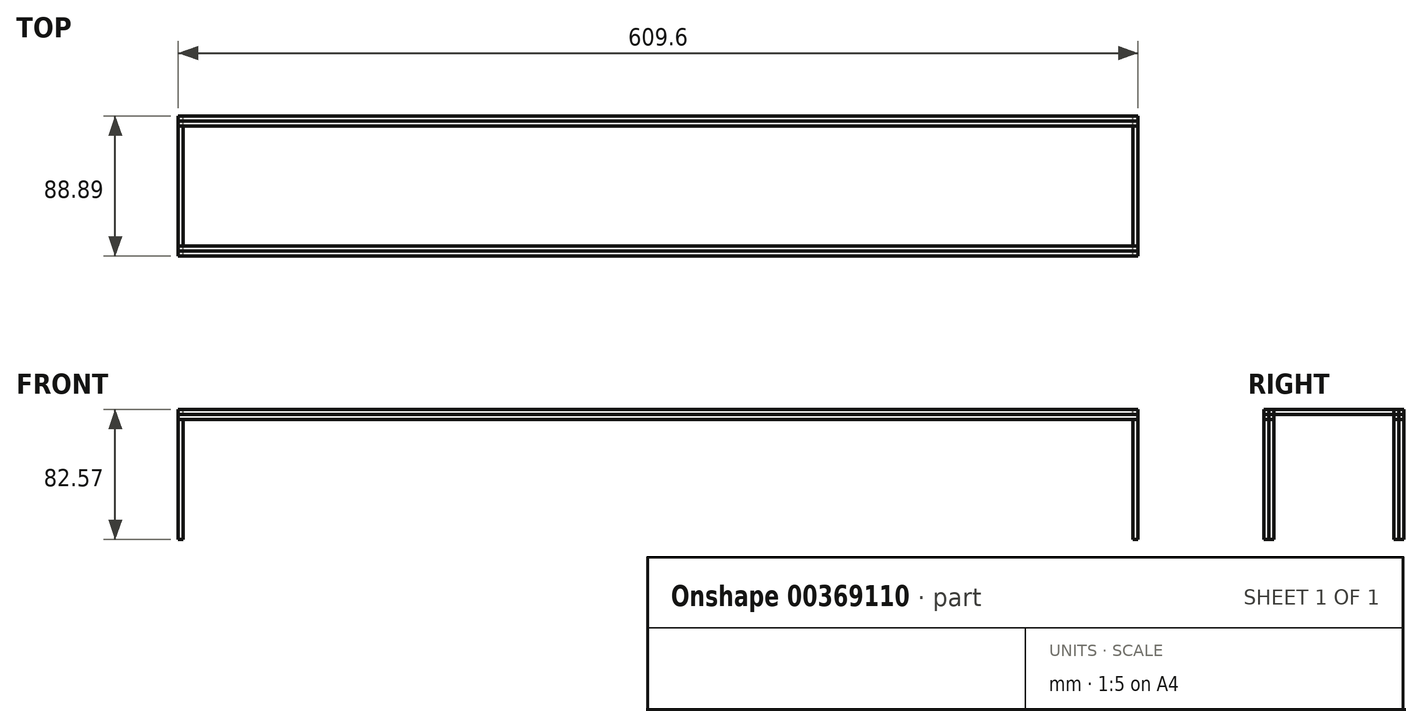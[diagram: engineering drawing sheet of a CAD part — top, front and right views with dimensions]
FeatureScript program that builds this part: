
annotation { "Feature Type Name" : "Feature", "Feature Type Description" : "" }
export const myFeature = defineFeature(function(context is Context, id is Id, definition is map)
    precondition{}
    {
        {
            var Q0;
            Q0=qCreatedBy(makeId("Front.planeOp"),FACE);
            var sketch = newSketch(context, id + "F0", { "sketchPlane" : qUnion([Q0])});
            skLineSegment(sketch, "E0.bottom", {"start": v(-296.3, -78.86) * mm, "end": v(313.3, -78.86) * mm});
            skLineSegment(sketch, "E0.top", {"start": v(-296.3, -75.69) * mm, "end": v(313.3, -75.69) * mm});
            skLineSegment(sketch, "E0.left", {"start": v(-296.3, -78.86) * mm, "end": v(-296.3, -75.69) * mm});
            skLineSegment(sketch, "E0.right", {"start": v(313.3, -78.86) * mm, "end": v(313.3, -75.69) * mm});
            skSolve(sketch);
        }
        {
            var Q0;
            Q0 = qSketchRegion(id + "F0", true);
            extrude(context, id + "F1", {"entities" : qUnion([Q0]), "depth" : 3.17 * mm});
        }
        {
            var Q0;
            Q0=makeQuery(id+"F1.opExtrude","SWEPT_BODY",BODY,{"disambiguationData":[OSD([sQuery(id+"F0.wireOp",EDGE,"E0.bottom"),sQuery(id+"F0.wireOp",EDGE,"E0.top"),sQuery(id+"F0.wireOp",EDGE,"E0.left"),sQuery(id+"F0.wireOp",EDGE,"E0.right")])]});
            transform(context, id + "F2", {"entities" : qUnion([Q0]), "transformType" : TransformType.TRANSLATION_3D, "dx" : 0 * mm, "dy" : 3.17 * mm, "dz" : 0 * mm, "makeCopy" : true});
        }
        {
            var Q0;
            Q0=makeQuery(id+"F1.opExtrude","SWEPT_BODY",BODY,{"disambiguationData":[OSD([sQuery(id+"F0.wireOp",EDGE,"E0.bottom"),sQuery(id+"F0.wireOp",EDGE,"E0.top"),sQuery(id+"F0.wireOp",EDGE,"E0.left"),sQuery(id+"F0.wireOp",EDGE,"E0.right")])]});
            transform(context, id + "F3", {"entities" : qUnion([Q0]), "transformType" : TransformType.TRANSLATION_3D, "dx" : 0 * mm, "dy" : 3.17 * mm, "dz" : 0 * mm, "makeCopy" : true});
        }
        {
            var Q0;
            Q0=makeQuery(id+"F1.opExtrude","SWEPT_BODY",BODY,{"disambiguationData":[OSD([sQuery(id+"F0.wireOp",EDGE,"E0.bottom"),sQuery(id+"F0.wireOp",EDGE,"E0.top"),sQuery(id+"F0.wireOp",EDGE,"E0.left"),sQuery(id+"F0.wireOp",EDGE,"E0.right")])]});
            transform(context, id + "F4", {"entities" : qUnion([Q0]), "transformType" : TransformType.TRANSLATION_3D, "dx" : 0 * mm, "dy" : 3.17 * mm, "dz" : 0 * mm, "makeCopy" : true});
        }
        {
            var Q0;
            Q0=makeQuery(id+"F1.opExtrude","SWEPT_BODY",BODY,{"disambiguationData":[OSD([sQuery(id+"F0.wireOp",EDGE,"E0.bottom"),sQuery(id+"F0.wireOp",EDGE,"E0.top"),sQuery(id+"F0.wireOp",EDGE,"E0.left"),sQuery(id+"F0.wireOp",EDGE,"E0.right")])]});
            transform(context, id + "F5", {"entities" : qUnion([Q0]), "transformType" : TransformType.TRANSLATION_3D, "dx" : 0 * mm, "dy" : 0 * mm, "dz" : 3.17 * mm, "makeCopy" : true});
        }
        {
            var Q0;
            Q0=makeQuery(id+"F1.opExtrude","SWEPT_BODY",BODY,{"disambiguationData":[OSD([sQuery(id+"F0.wireOp",EDGE,"E0.bottom"),sQuery(id+"F0.wireOp",EDGE,"E0.top"),sQuery(id+"F0.wireOp",EDGE,"E0.left"),sQuery(id+"F0.wireOp",EDGE,"E0.right")])]});
            transform(context, id + "F6", {"entities" : qUnion([Q0]), "transformType" : TransformType.TRANSLATION_3D, "dx" : 0 * mm, "dy" : 0 * mm, "dz" : 3.17 * mm, "makeCopy" : true});
        }
        {
            var Q0;
            Q0=makeQuery(id+"F1.opExtrude","SWEPT_BODY",BODY,{"disambiguationData":[OSD([sQuery(id+"F0.wireOp",EDGE,"E0.bottom"),sQuery(id+"F0.wireOp",EDGE,"E0.top"),sQuery(id+"F0.wireOp",EDGE,"E0.left"),sQuery(id+"F0.wireOp",EDGE,"E0.right")])]});
            transform(context, id + "F7", {"entities" : qUnion([Q0]), "transformType" : TransformType.TRANSLATION_3D, "dx" : 0 * mm, "dy" : 0 * mm, "dz" : 3.17 * mm, "makeCopy" : true});
        }
        {
            var Q0;
            Q0=makeQuery(id+"F7.opPattern","COPY",BODY,{"derivedFrom":makeQuery(id+"F1.opExtrude","SWEPT_BODY",BODY,{"disambiguationData":[OSD([sQuery(id+"F0.wireOp",EDGE,"E0.bottom"),sQuery(id+"F0.wireOp",EDGE,"E0.top"),sQuery(id+"F0.wireOp",EDGE,"E0.left"),sQuery(id+"F0.wireOp",EDGE,"E0.right")])]}),"instanceName":"1"});
            deleteBodies(context, id + "F8", {"entities" : qUnion([Q0])});
        }
        {
            var Q0;
            Q0=makeQuery(id+"F6.opPattern","COPY",BODY,{"derivedFrom":makeQuery(id+"F1.opExtrude","SWEPT_BODY",BODY,{"disambiguationData":[OSD([sQuery(id+"F0.wireOp",EDGE,"E0.bottom"),sQuery(id+"F0.wireOp",EDGE,"E0.top"),sQuery(id+"F0.wireOp",EDGE,"E0.left"),sQuery(id+"F0.wireOp",EDGE,"E0.right")])]}),"instanceName":"1"});
            deleteBodies(context, id + "F9", {"entities" : qUnion([Q0])});
        }
        {
            var Q0;
            Q0=makeQuery(id+"F4.opPattern","COPY",BODY,{"derivedFrom":makeQuery(id+"F1.opExtrude","SWEPT_BODY",BODY,{"disambiguationData":[OSD([sQuery(id+"F0.wireOp",EDGE,"E0.bottom"),sQuery(id+"F0.wireOp",EDGE,"E0.top"),sQuery(id+"F0.wireOp",EDGE,"E0.left"),sQuery(id+"F0.wireOp",EDGE,"E0.right")])]}),"instanceName":"1"});
            transform(context, id + "F10", {"entities" : qUnion([Q0]), "transformType" : TransformType.TRANSLATION_3D, "dx" : 0 * mm, "dy" : 0 * mm, "dz" : 3.17 * mm, "makeCopy" : true});
        }
        {
            var Q0;
            Q0=qCreatedBy(makeId("Front.planeOp"),FACE);
            var sketch = newSketch(context, id + "F11", { "sketchPlane" : qUnion([Q0])});
            skLineSegment(sketch, "E1.bottom", {"start": v(-296.3, -78.86) * mm, "end": v(-293.12, -78.86) * mm});
            skLineSegment(sketch, "E1.top", {"start": v(-296.3, -155.06) * mm, "end": v(-293.12, -155.06) * mm});
            skLineSegment(sketch, "E1.left", {"start": v(-296.3, -78.86) * mm, "end": v(-296.3, -155.06) * mm});
            skLineSegment(sketch, "E1.right", {"start": v(-293.12, -78.86) * mm, "end": v(-293.12, -155.06) * mm});
            skSolve(sketch);
        }
        {
            var Q0;
            Q0=makeQuery(id+"F11.imprint","IMPRINT",FACE,{"disambiguationData":[TD([[makeQuery(id+"F11.imprint","IMPRINT",EDGE,{"derivedFrom":sQuery(id+"F11.wireOp",EDGE,"E1.bottom")}),-1.0]])]});
            extrude(context, id + "F12", {"entities" : qUnion([Q0]), "depth" : 3.17 * mm});
        }
        {
            var Q0;
            Q0=makeQuery(id+"F12.opExtrude","SWEPT_BODY",BODY,{"disambiguationData":[OSD([sQuery(id+"F11.wireOp",EDGE,"E1.bottom"),sQuery(id+"F11.wireOp",EDGE,"E1.top"),sQuery(id+"F11.wireOp",EDGE,"E1.left"),sQuery(id+"F11.wireOp",EDGE,"E1.right")])]});
            transform(context, id + "F13", {"entities" : qUnion([Q0]), "transformType" : TransformType.TRANSLATION_3D, "dx" : 0 * mm, "dy" : 3.17 * mm, "dz" : 0 * mm, "makeCopy" : true});
        }
        {
            var Q0;
            Q0=makeQuery(id+"F12.opExtrude","SWEPT_BODY",BODY,{"disambiguationData":[OSD([sQuery(id+"F11.wireOp",EDGE,"E1.bottom"),sQuery(id+"F11.wireOp",EDGE,"E1.top"),sQuery(id+"F11.wireOp",EDGE,"E1.left"),sQuery(id+"F11.wireOp",EDGE,"E1.right")])]});
            transform(context, id + "F14", {"entities" : qUnion([Q0]), "transformType" : TransformType.TRANSLATION_3D, "dx" : 606.42 * mm, "dy" : 0 * mm, "dz" : 0 * mm, "makeCopy" : true});
        }
        {
            var Q0;
            Q0=makeQuery(id+"F13.opPattern","COPY",BODY,{"derivedFrom":makeQuery(id+"F12.opExtrude","SWEPT_BODY",BODY,{"disambiguationData":[OSD([sQuery(id+"F11.wireOp",EDGE,"E1.bottom"),sQuery(id+"F11.wireOp",EDGE,"E1.top"),sQuery(id+"F11.wireOp",EDGE,"E1.left"),sQuery(id+"F11.wireOp",EDGE,"E1.right")])]}),"instanceName":"1"});
            transform(context, id + "F15", {"entities" : qUnion([Q0]), "transformType" : TransformType.TRANSLATION_3D, "dx" : 606.42 * mm, "dy" : 0 * mm, "dz" : 0 * mm, "makeCopy" : true});
        }
        {
            var Q0;
            Q0=makeQuery(id+"F1.opExtrude","SWEPT_BODY",BODY,{"disambiguationData":[OSD([sQuery(id+"F0.wireOp",EDGE,"E0.bottom"),sQuery(id+"F0.wireOp",EDGE,"E0.top"),sQuery(id+"F0.wireOp",EDGE,"E0.left"),sQuery(id+"F0.wireOp",EDGE,"E0.right")])]});
            var Q1;
            Q1=makeQuery(id+"F2.opPattern","COPY",BODY,{"derivedFrom":makeQuery(id+"F1.opExtrude","SWEPT_BODY",BODY,{"disambiguationData":[OSD([sQuery(id+"F0.wireOp",EDGE,"E0.bottom"),sQuery(id+"F0.wireOp",EDGE,"E0.top"),sQuery(id+"F0.wireOp",EDGE,"E0.left"),sQuery(id+"F0.wireOp",EDGE,"E0.right")])]}),"instanceName":"1"});
            var Q2;
            Q2=makeQuery(id+"F3.opPattern","COPY",BODY,{"derivedFrom":makeQuery(id+"F1.opExtrude","SWEPT_BODY",BODY,{"disambiguationData":[OSD([sQuery(id+"F0.wireOp",EDGE,"E0.bottom"),sQuery(id+"F0.wireOp",EDGE,"E0.top"),sQuery(id+"F0.wireOp",EDGE,"E0.left"),sQuery(id+"F0.wireOp",EDGE,"E0.right")])]}),"instanceName":"1"});
            var Q3;
            Q3=makeQuery(id+"F4.opPattern","COPY",BODY,{"derivedFrom":makeQuery(id+"F1.opExtrude","SWEPT_BODY",BODY,{"disambiguationData":[OSD([sQuery(id+"F0.wireOp",EDGE,"E0.bottom"),sQuery(id+"F0.wireOp",EDGE,"E0.top"),sQuery(id+"F0.wireOp",EDGE,"E0.left"),sQuery(id+"F0.wireOp",EDGE,"E0.right")])]}),"instanceName":"1"});
            var Q4;
            Q4=makeQuery(id+"F5.opPattern","COPY",BODY,{"derivedFrom":makeQuery(id+"F1.opExtrude","SWEPT_BODY",BODY,{"disambiguationData":[OSD([sQuery(id+"F0.wireOp",EDGE,"E0.bottom"),sQuery(id+"F0.wireOp",EDGE,"E0.top"),sQuery(id+"F0.wireOp",EDGE,"E0.left"),sQuery(id+"F0.wireOp",EDGE,"E0.right")])]}),"instanceName":"1"});
            var Q5;
            Q5=makeQuery(id+"F10.opPattern","COPY",BODY,{"derivedFrom":makeQuery(id+"F4.opPattern","COPY",BODY,{"derivedFrom":makeQuery(id+"F1.opExtrude","SWEPT_BODY",BODY,{"disambiguationData":[OSD([sQuery(id+"F0.wireOp",EDGE,"E0.bottom"),sQuery(id+"F0.wireOp",EDGE,"E0.top"),sQuery(id+"F0.wireOp",EDGE,"E0.left"),sQuery(id+"F0.wireOp",EDGE,"E0.right")])]}),"instanceName":"1"}),"instanceName":"1"});
            var Q6;
            Q6=makeQuery(id+"F12.opExtrude","SWEPT_BODY",BODY,{"disambiguationData":[OSD([sQuery(id+"F11.wireOp",EDGE,"E1.bottom"),sQuery(id+"F11.wireOp",EDGE,"E1.top"),sQuery(id+"F11.wireOp",EDGE,"E1.left"),sQuery(id+"F11.wireOp",EDGE,"E1.right")])]});
            var Q7;
            Q7=makeQuery(id+"F13.opPattern","COPY",BODY,{"derivedFrom":makeQuery(id+"F12.opExtrude","SWEPT_BODY",BODY,{"disambiguationData":[OSD([sQuery(id+"F11.wireOp",EDGE,"E1.bottom"),sQuery(id+"F11.wireOp",EDGE,"E1.top"),sQuery(id+"F11.wireOp",EDGE,"E1.left"),sQuery(id+"F11.wireOp",EDGE,"E1.right")])]}),"instanceName":"1"});
            var Q8;
            Q8=makeQuery(id+"F14.opPattern","COPY",BODY,{"derivedFrom":makeQuery(id+"F12.opExtrude","SWEPT_BODY",BODY,{"disambiguationData":[OSD([sQuery(id+"F11.wireOp",EDGE,"E1.bottom"),sQuery(id+"F11.wireOp",EDGE,"E1.top"),sQuery(id+"F11.wireOp",EDGE,"E1.left"),sQuery(id+"F11.wireOp",EDGE,"E1.right")])]}),"instanceName":"1"});
            var Q9;
            Q9=makeQuery(id+"F15.opPattern","COPY",BODY,{"derivedFrom":makeQuery(id+"F13.opPattern","COPY",BODY,{"derivedFrom":makeQuery(id+"F12.opExtrude","SWEPT_BODY",BODY,{"disambiguationData":[OSD([sQuery(id+"F11.wireOp",EDGE,"E1.bottom"),sQuery(id+"F11.wireOp",EDGE,"E1.top"),sQuery(id+"F11.wireOp",EDGE,"E1.left"),sQuery(id+"F11.wireOp",EDGE,"E1.right")])]}),"instanceName":"1"}),"instanceName":"1"});
            transform(context, id + "F16", {"entities" : qUnion([Q0, Q1, Q2, Q3, Q4, Q5, Q6, Q7, Q8, Q9]), "transformType" : TransformType.TRANSLATION_3D, "dx" : 0 * mm, "dy" : 82.55 * mm, "dz" : 0 * mm, "makeCopy" : true});
        }
        {
            var Q0;
            Q0=makeQuery(id+"F15.opPattern","COPY",FACE,{"derivedFrom":makeQuery(id+"F13.opPattern","COPY",FACE,{"derivedFrom":makeQuery(id+"F12.opExtrude","SWEPT_FACE",FACE,{"disambiguationData":[OSD([sQuery(id+"F11.wireOp",EDGE,"E1.right")])]}),"instanceName":"1"}),"instanceName":"1"});
            cPlane(context, id + "F17", {"entities" : qUnion([Q0]), "cplaneType" : CPlaneType.OFFSET, "offset" : 0 * mm, "width" : 152.4 * mm, "height" : 152.4 * mm});
        }
        {
            var Q0;
            Q0=qCreatedBy(id+"F17.planeOp",FACE);
            var sketch = newSketch(context, id + "F18", { "sketchPlane" : qUnion([Q0])});
            skLineSegment(sketch, "E2.bottom", {"start": v(3.2, -75.77) * mm, "end": v(79.27, -75.77) * mm});
            skLineSegment(sketch, "E2.top", {"start": v(3.2, -72.5) * mm, "end": v(79.27, -72.5) * mm});
            skLineSegment(sketch, "E2.left", {"start": v(3.2, -75.77) * mm, "end": v(3.2, -72.5) * mm});
            skLineSegment(sketch, "E2.right", {"start": v(79.27, -75.77) * mm, "end": v(79.27, -72.5) * mm});
            skSolve(sketch);
        }
        {
            var Q0;
            Q0 = qSketchRegion(id + "F18", true);
            extrude(context, id + "F19", {"entities" : qUnion([Q0]), "depth" : -3.17 * mm});
        }
        {
            var Q0;
            Q0=makeQuery(id+"F19.opExtrude","SWEPT_BODY",BODY,{"disambiguationData":[OSD([sQuery(id+"F18.wireOp",EDGE,"E2.bottom"),sQuery(id+"F18.wireOp",EDGE,"E2.top"),sQuery(id+"F18.wireOp",EDGE,"E2.left"),sQuery(id+"F18.wireOp",EDGE,"E2.right")])]});
            transform(context, id + "F20", {"entities" : qUnion([Q0]), "transformType" : TransformType.TRANSLATION_3D, "dx" : -606.42 * mm, "dy" : 0 * mm, "dz" : 0 * mm, "makeCopy" : true});
        }
    });
